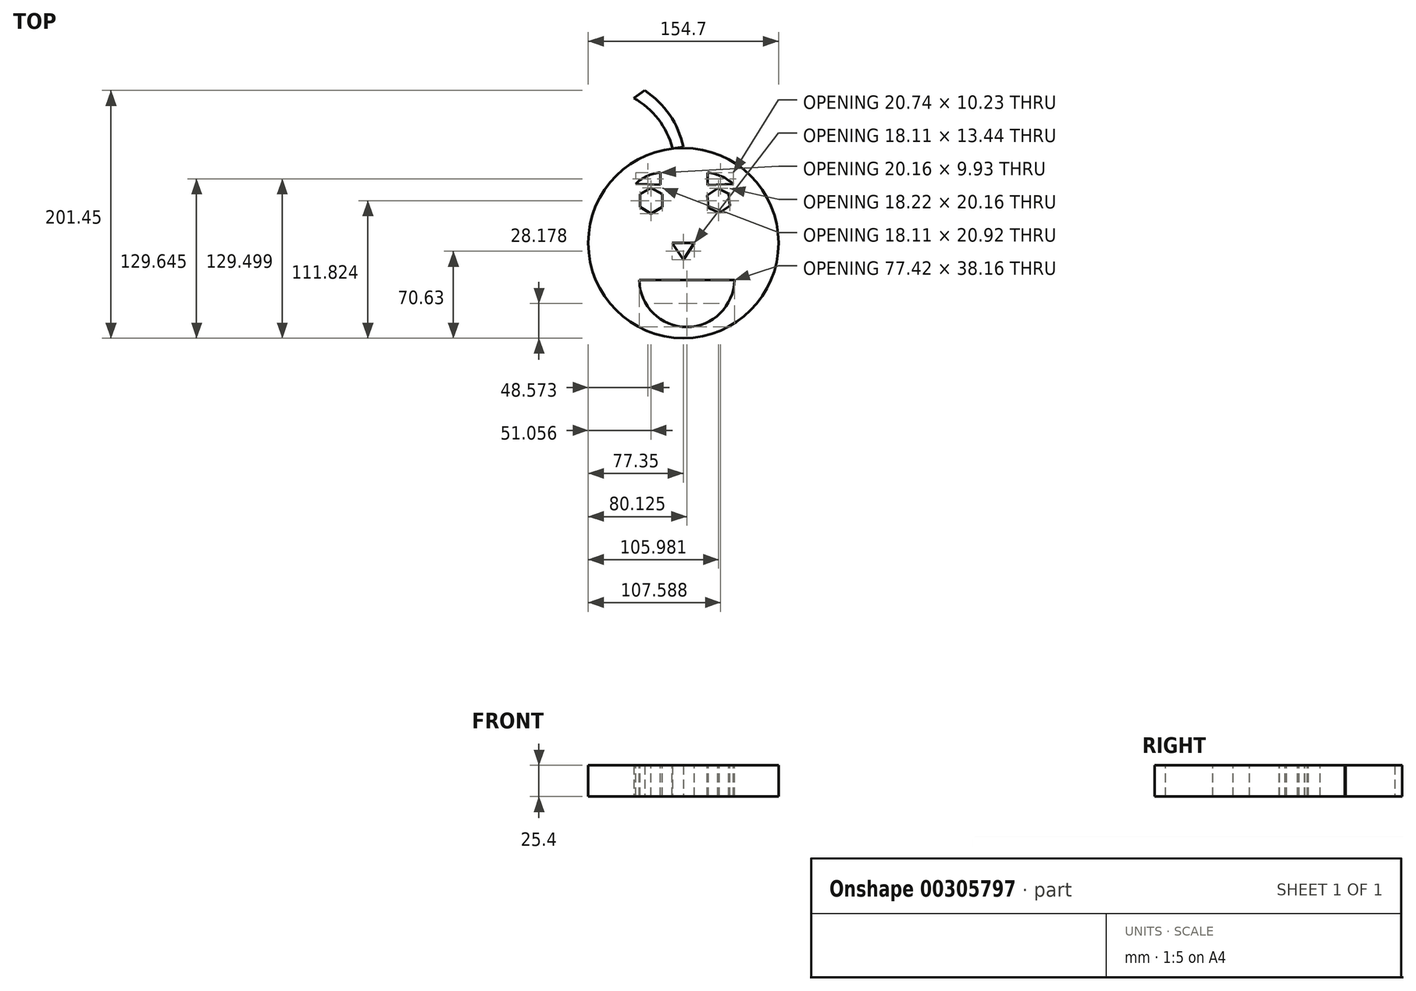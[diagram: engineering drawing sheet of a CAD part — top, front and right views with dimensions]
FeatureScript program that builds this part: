
annotation { "Feature Type Name" : "Feature", "Feature Type Description" : "" }
export const myFeature = defineFeature(function(context is Context, id is Id, definition is map)
    precondition{}
    {
        {
            var Q0;
            Q0=qCreatedBy(makeId("Top.planeOp"),FACE);
            var sketch = newSketch(context, id + "F0", { "sketchPlane" : qUnion([Q0])});
            skCircle(sketch, "E0", {"center": v(0, 0) * mm, "radius": 77.35 * mm});
            skLineSegment(sketch, "E1", {"start": v(-34.64, 69.16) * mm, "end": v(-1.68, 91.99) * mm});
            skLineSegment(sketch, "E2", {"start": v(-1.68, 91.99) * mm, "end": v(25.36, 73.08) * mm});
            skSolve(sketch);
        }
        {
            var Q0;
            Q0=makeQuery(id+"F0.imprint","IMPRINT",FACE,{"disambiguationData":[TD([[makeQuery(id+"F0.imprint","IMPRINT",EDGE,{"derivedFrom":sQuery(id+"F0.wireOp",EDGE,"E0")}),1.0]])]});
            extrude(context, id + "F1", {"entities" : qUnion([Q0]), "depth" : 25.4 * mm});
        }
        {
            var Q0;
            Q0=makeQuery(id+"F1.opExtrude","CAP_FACE",FACE,{"disambiguationData":[OSD([sQuery(id+"F0.wireOp",EDGE,"E0")])],"isStart":false});
            var sketch = newSketch(context, id + "F2", { "sketchPlane" : qUnion([Q0])});
            skLineSegment(sketch, "E3", {"start": v(-9.06, 0) * mm, "end": v(9.06, 0) * mm});
            skLineSegment(sketch, "E4", {"start": v(9.06, 0) * mm, "end": v(0, -13.44) * mm});
            skLineSegment(sketch, "E5", {"start": v(0, -13.44) * mm, "end": v(-9.06, 0) * mm});
            skLineSegment(sketch, "E6", {"start": v(-9.06, 0) * mm, "end": v(66.9, -10.8) * mm});
            skSolve(sketch);
        }
        {
            var Q0;
            Q0 = qSketchRegion(id + "F2", true);
            extrude(context, id + "F3", {"entities" : qUnion([Q0]), "operationType" : NewBodyOperationType.REMOVE, "oppositeDirection" : true, "depth" : 25.4 * mm});
        }
        {
            var Q0;
            Q0=makeQuery(id+"F1.opExtrude","CAP_FACE",FACE,{"disambiguationData":[OSD([sQuery(id+"F0.wireOp",EDGE,"E0")])],"isStart":false});
            var sketch = newSketch(context, id + "F4", { "sketchPlane" : qUnion([Q0])});
            skArc(sketch, "E7", {"start": v(-18.7, 57.26) * mm, "mid": v(-29.67, 54.5) * mm, "end": v(-38.86, 47.91) * mm});
            skLineSegment(sketch, "E8", {"start": v(-18.7, 57.26) * mm, "end": v(-18.7, 47.33) * mm});
            skLineSegment(sketch, "E9", {"start": v(-18.7, 47.33) * mm, "end": v(-38.86, 47.91) * mm});
            skArc(sketch, "E10", {"start": v(40.6, 47.91) * mm, "mid": v(30.98, 54.22) * mm, "end": v(19.87, 57.26) * mm});
            skLineSegment(sketch, "E11", {"start": v(19.87, 57.26) * mm, "end": v(19.87, 47.04) * mm});
            skLineSegment(sketch, "E12", {"start": v(19.87, 47.04) * mm, "end": v(40.6, 47.91) * mm});
            skSolve(sketch);
        }
        {
            var Q0;
            Q0 = qSketchRegion(id + "F4", true);
            extrude(context, id + "F5", {"entities" : qUnion([Q0]), "operationType" : NewBodyOperationType.REMOVE, "oppositeDirection" : true, "depth" : 25.4 * mm});
        }
        {
            var Q0;
            Q0=makeQuery(id+"F1.opExtrude","CAP_FACE",FACE,{"disambiguationData":[OSD([sQuery(id+"F0.wireOp",EDGE,"E0")])],"isStart":false});
            var sketch = newSketch(context, id + "F6", { "sketchPlane" : qUnion([Q0])});
            skCircle(sketch, "E13.cCircle", {"center": v(-26.3, 34.47) * mm, "radius": 9.06 * mm, "construction": true});
            skLineSegment(sketch, "E13.0", {"start": v(-17.24, 39.7) * mm, "end": v(-17.24, 29.25) * mm});
            skLineSegment(sketch, "E13.1", {"start": v(-17.24, 29.25) * mm, "end": v(-26.3, 24.02) * mm});
            skLineSegment(sketch, "E13.2", {"start": v(-26.3, 24.02) * mm, "end": v(-35.35, 29.25) * mm});
            skLineSegment(sketch, "E13.3", {"start": v(-35.35, 29.25) * mm, "end": v(-35.35, 39.7) * mm});
            skLineSegment(sketch, "E13.4", {"start": v(-35.35, 39.7) * mm, "end": v(-26.3, 44.93) * mm});
            skLineSegment(sketch, "E13.5", {"start": v(-26.3, 44.93) * mm, "end": v(-17.24, 39.7) * mm});
            skPoint(sketch, "E13.0.midPoint", {"position": v(-17.24, 34.47) * mm});
            skCircle(sketch, "E14.cCircle", {"center": v(28.63, 34.47) * mm, "radius": 8.75 * mm, "construction": true});
            skLineSegment(sketch, "E14.0", {"start": v(27.87, 44.55) * mm, "end": v(36.98, 40.17) * mm});
            skLineSegment(sketch, "E14.1", {"start": v(36.98, 40.17) * mm, "end": v(37.74, 30.09) * mm});
            skLineSegment(sketch, "E14.2", {"start": v(37.74, 30.09) * mm, "end": v(29.39, 24.4) * mm});
            skLineSegment(sketch, "E14.3", {"start": v(29.39, 24.4) * mm, "end": v(20.28, 28.78) * mm});
            skLineSegment(sketch, "E14.4", {"start": v(20.28, 28.78) * mm, "end": v(19.52, 38.86) * mm});
            skLineSegment(sketch, "E14.5", {"start": v(19.52, 38.86) * mm, "end": v(27.87, 44.55) * mm});
            skPoint(sketch, "E14.0.midPoint", {"position": v(32.43, 42.36) * mm});
            skSolve(sketch);
        }
        {
            var Q0;
            Q0 = qSketchRegion(id + "F6", true);
            extrude(context, id + "F7", {"entities" : qUnion([Q0]), "operationType" : NewBodyOperationType.REMOVE, "oppositeDirection" : true, "depth" : 25.4 * mm});
        }
        {
            var Q0;
            Q0=makeQuery(id+"F1.opExtrude","CAP_FACE",FACE,{"disambiguationData":[OSD([sQuery(id+"F0.wireOp",EDGE,"E0")])],"isStart":false});
            var sketch = newSketch(context, id + "F8", { "sketchPlane" : qUnion([Q0])});
            skLineSegment(sketch, "E15", {"start": v(-35.93, -30.1) * mm, "end": v(41.49, -30.1) * mm});
            skArc(sketch, "E16", {"start": v(-35.93, -30.1) * mm, "mid": v(2.78, -68.25) * mm, "end": v(41.49, -30.1) * mm});
            skSolve(sketch);
        }
        {
            var Q0;
            Q0 = qSketchRegion(id + "F8", true);
            extrude(context, id + "F9", {"entities" : qUnion([Q0]), "operationType" : NewBodyOperationType.REMOVE, "oppositeDirection" : true, "depth" : 25.4 * mm});
        }
        {
            var Q0;
            Q0=qCreatedBy(makeId("Top.planeOp"),FACE);
            var sketch = newSketch(context, id + "F10", { "sketchPlane" : qUnion([Q0])});
            skArc(sketch, "E17", {"start": v(-8.97, 77.03) * mm, "mid": v(-20.38, 100.82) * mm, "end": v(-40.45, 117.96) * mm});
            skArc(sketch, "E18", {"start": v(0, 78.05) * mm, "mid": v(-11.14, 104.18) * mm, "end": v(-31.4, 124.1) * mm});
            skLineSegment(sketch, "E19", {"start": v(-40.45, 117.96) * mm, "end": v(-31.4, 124.1) * mm});
            skLineSegment(sketch, "E20", {"start": v(-8.97, 77.03) * mm, "end": v(0, 78.05) * mm});
            skSolve(sketch);
        }
        {
            var Q0;
            Q0 = qSketchRegion(id + "F10", true);
            extrude(context, id + "F11", {"entities" : qUnion([Q0]), "depth" : 25.4 * mm});
        }
    });
